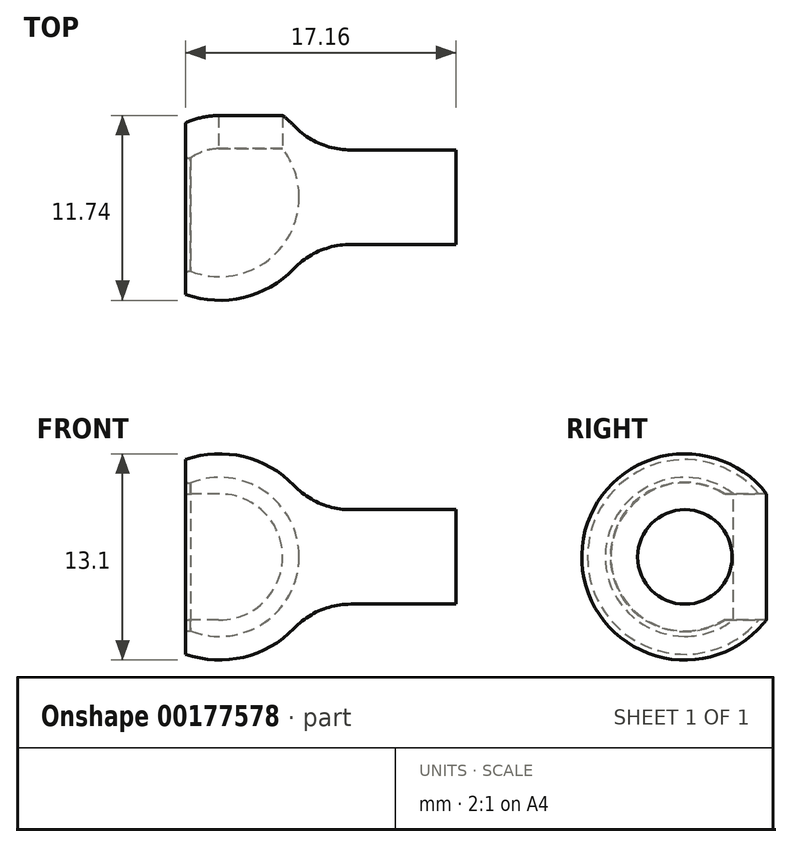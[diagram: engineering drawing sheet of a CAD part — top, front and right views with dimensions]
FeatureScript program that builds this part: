
annotation { "Feature Type Name" : "Feature", "Feature Type Description" : "" }
export const myFeature = defineFeature(function(context is Context, id is Id, definition is map)
    precondition{}
    {
        {
            var Q0;
            Q0=qCreatedBy(makeId("Front.planeOp"),FACE);
            var sketch = newSketch(context, id + "F0", { "sketchPlane" : qUnion([Q0])});
            skLineSegment(sketch, "E0", {"start": v(0, 0) * mm, "end": v(-9.95, 0) * mm});
            skLineSegment(sketch, "E1", {"start": v(0, 0) * mm, "end": v(0, -3) * mm});
            skLineSegment(sketch, "E2.0", {"start": v(0, -3) * mm, "end": v(-9.18, -3) * mm});
            skArc(sketch, "E3.trimOffspring", {"start": v(-17.16, -6.18) * mm, "mid": v(-12.58, -6.08) * mm, "end": v(-9.18, -3) * mm});
            skArc(sketch, "E4.trimOffspring", {"start": v(-16.85, -4.7) * mm, "mid": v(-12.16, -4.17) * mm, "end": v(-9.95, 0) * mm});
            skLineSegment(sketch, "E5.trimOffspring", {"start": v(-16.85, -4.7) * mm, "end": v(-16.91, -4.7) * mm});
            skPoint(sketch, "E6.visualSharp", {"position": v(-19.56, -4.7) * mm});
            skArc(sketch, "E6.filletArc", {"start": v(-16.91, -4.7) * mm, "mid": v(-17.04, -4.71) * mm, "end": v(-17.16, -4.74) * mm});
            skLineSegment(sketch, "E7", {"start": v(-17.16, -6.18) * mm, "end": v(-17.16, -4.74) * mm});
            skSolve(sketch);
        }
        {
            var Q0;
            Q0=qSketchRegion(id+"F0",true);
            var Q1;
            Q1=sQuery(id+"F0.wireOp",EDGE,"E0");
            revolve(context, id + "F1", {"entities" : qUnion([Q0]), "axis" : qUnion([Q1]), "revolveType" : RevolveType.FULL});
        }
        {
            var Q0;
            Q0=qCreatedBy(makeId("Front.planeOp"),FACE);
            var sketch = newSketch(context, id + "F2", { "sketchPlane" : qUnion([Q0])});
            skPoint(sketch, "E8.center.orphan", {"position": v(-13.79, 0) * mm});
            skArc(sketch, "E9", {"start": v(-15.06, -4) * mm, "mid": v(-11, -0.03) * mm, "end": v(-15, 4) * mm});
            skLineSegment(sketch, "E10", {"start": v(-15.06, -4) * mm, "end": v(-18.56, -4) * mm});
            skLineSegment(sketch, "E11", {"start": v(-15, 4) * mm, "end": v(-18.58, 4) * mm});
            skPoint(sketch, "E12.orphan", {"position": v(-15, 5.07) * mm});
            skLineSegment(sketch, "E13", {"start": v(-18.58, 4) * mm, "end": v(-18.56, -4) * mm});
            skPoint(sketch, "E13.endSnap0", {"position": v(-19.2, -4) * mm});
            skPoint(sketch, "E14.orphan", {"position": v(-22.15, 3.99) * mm});
            skPoint(sketch, "E15.orphan", {"position": v(-23.34, -4) * mm});
            skSolve(sketch);
        }
        {
            var Q0;
            Q0=qSketchRegion(id+"F2",true);
            extrude(context, id + "F3", {"entities" : qUnion([Q0]), "operationType" : NewBodyOperationType.REMOVE, "oppositeDirection" : true, "depth" : 25 * mm});
        }
        {
            var Q0;
            Q0=makeQuery(id+"F1.opRevolve","SWEPT_EDGE",EDGE,{"disambiguationData":[OSD([sQuery(id+"F0.wireOp",EDGE,"E2.0"),sQuery(id+"F0.wireOp",EDGE,"E3.trimOffspring")])]});
            fillet(context, id + "F4", {"entities" : qUnion([Q0]), "radius" : 5 * mm, "tangentPropagation" : true, "allowEdgeOverflow" : false});
        }
    });
